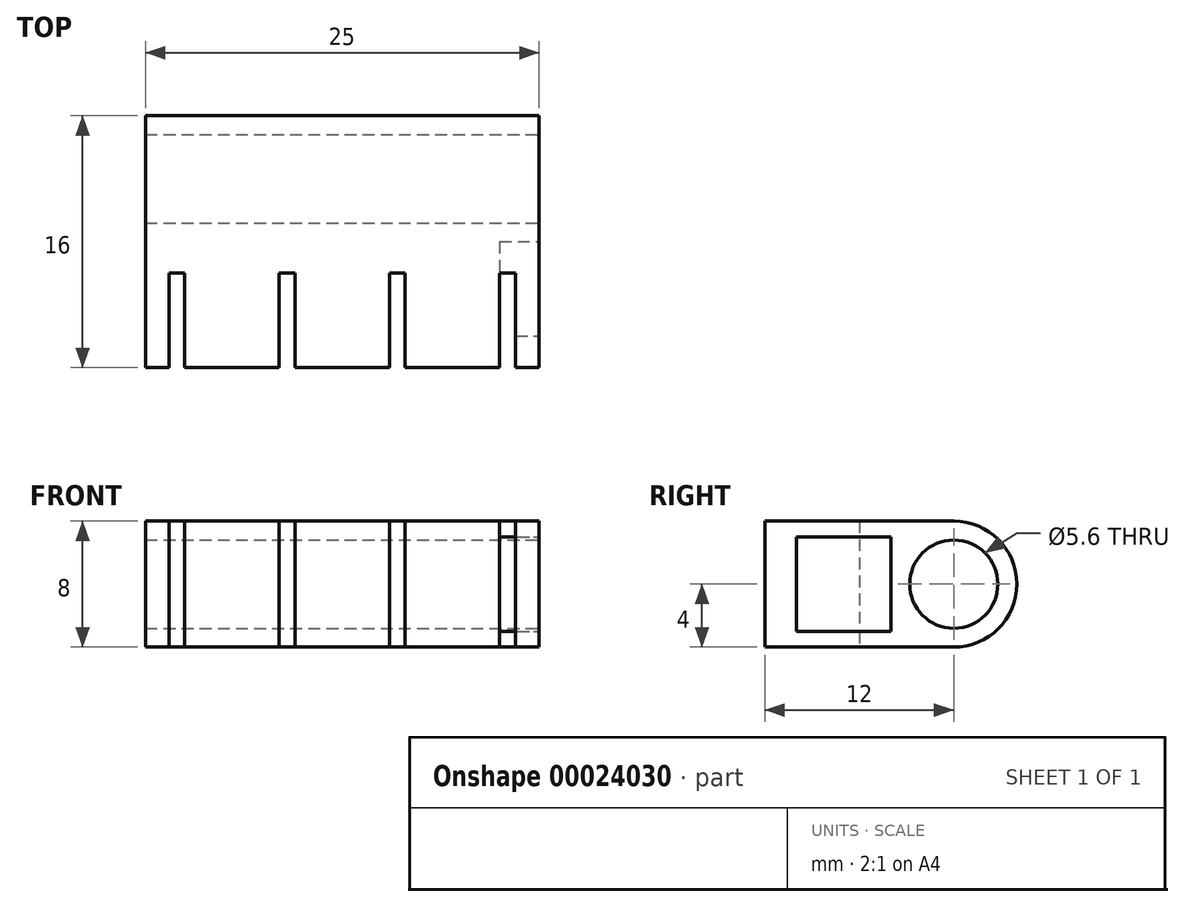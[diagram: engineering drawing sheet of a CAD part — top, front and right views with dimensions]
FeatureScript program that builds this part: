
annotation { "Feature Type Name" : "Feature", "Feature Type Description" : "" }
export const myFeature = defineFeature(function(context is Context, id is Id, definition is map)
    precondition{}
    {
        {
            var Q0;
            Q0=qCreatedBy(makeId("Top.planeOp"),FACE);
            var sketch = newSketch(context, id + "F0", { "sketchPlane" : qUnion([Q0])});
            skLineSegment(sketch, "E0.rect.bottom", {"start": v(-12.5, -5) * mm, "end": v(12.5, -5) * mm});
            skLineSegment(sketch, "E0.rect.top", {"start": v(-12.5, 5) * mm, "end": v(12.5, 5) * mm});
            skLineSegment(sketch, "E0.rect.left", {"start": v(-12.5, -5) * mm, "end": v(-12.5, 5) * mm});
            skLineSegment(sketch, "E0.rect.right", {"start": v(12.5, -5) * mm, "end": v(12.5, 5) * mm});
            skPoint(sketch, "E0.rect.middle", {"position": v(0, 0) * mm});
            skLineSegment(sketch, "E1.bottom", {"start": v(-3, -5) * mm, "end": v(-4, -5) * mm});
            skLineSegment(sketch, "E1.top", {"start": v(-3, 1) * mm, "end": v(-4, 1) * mm});
            skLineSegment(sketch, "E1.left", {"start": v(-3, -5) * mm, "end": v(-3, 1) * mm});
            skLineSegment(sketch, "E1.right", {"start": v(-4, -5) * mm, "end": v(-4, 1) * mm});
            skLineSegment(sketch, "E2.0.MirrorCS", {"start": v(3, -5) * mm, "end": v(3, 1) * mm});
            skLineSegment(sketch, "E3.0.MirrorCS", {"start": v(3, 1) * mm, "end": v(4, 1) * mm});
            skLineSegment(sketch, "E4.0.MirrorCS", {"start": v(4, -5) * mm, "end": v(4, 1) * mm});
            skLineSegment(sketch, "E5", {"start": v(-3.5, 1) * mm, "end": v(-3.5, -6.52) * mm, "construction": true});
            skLineSegment(sketch, "E6.0.MirrorCS", {"start": v(-10, -5) * mm, "end": v(-10, 1) * mm});
            skLineSegment(sketch, "E7.0.MirrorCS", {"start": v(-10, 1) * mm, "end": v(-11, 1) * mm});
            skLineSegment(sketch, "E8.0.MirrorCS", {"start": v(-11, -5) * mm, "end": v(-11, 1) * mm});
            skLineSegment(sketch, "E9", {"start": v(3.5, 1) * mm, "end": v(3.5, -5) * mm, "construction": true});
            skLineSegment(sketch, "E10.0.MirrorCS", {"start": v(11, -5) * mm, "end": v(11, 1) * mm});
            skLineSegment(sketch, "E11.0.MirrorCS", {"start": v(10, -5) * mm, "end": v(10, 1) * mm});
            skLineSegment(sketch, "E12.0.MirrorCS", {"start": v(10, 1) * mm, "end": v(11, 1) * mm});
            skSolve(sketch);
        }
        {
            var Q0;
            Q0=makeQuery(id+"F0.imprint","IMPRINT",FACE,{"disambiguationData":[TD([[makeQuery(id+"F0.imprint","IMPRINT",EDGE,{"derivedFrom":sQuery(id+"F0.wireOp",EDGE,"E0.rect.top")}),-1.0]])]});
            extrude(context, id + "F1", {"entities" : qUnion([Q0]), "depth" : 8 * mm});
        }
        {
            var Q0;
            Q0=makeQuery(id+"F1.opExtrude","SWEPT_FACE",FACE,{"disambiguationData":[OSD([sQuery(id+"F0.wireOp",EDGE,"E0.rect.right")])]});
            var sketch = newSketch(context, id + "F2", { "sketchPlane" : qUnion([Q0])});
            skLineSegment(sketch, "E13", {"start": v(5, 4) * mm, "end": v(-5, 4) * mm, "construction": true});
            skLineSegment(sketch, "E14", {"start": v(0, 8) * mm, "end": v(0, 0) * mm, "construction": true});
            skLineSegment(sketch, "E15.rect.bottom", {"start": v(3, 7) * mm, "end": v(-3, 7) * mm});
            skLineSegment(sketch, "E15.rect.top", {"start": v(3, 1) * mm, "end": v(-3, 1) * mm});
            skLineSegment(sketch, "E15.rect.left", {"start": v(3, 7) * mm, "end": v(3, 1) * mm});
            skLineSegment(sketch, "E15.rect.right", {"start": v(-3, 7) * mm, "end": v(-3, 1) * mm});
            skPoint(sketch, "E15.rect.middle", {"position": v(0, 4) * mm});
            skSolve(sketch);
        }
        {
            var Q0;
            Q0=makeQuery(id+"F2.imprint","IMPRINT",FACE,{"disambiguationData":[TD([[makeQuery(id+"F2.imprint","IMPRINT",EDGE,{"derivedFrom":sQuery(id+"F2.wireOp",EDGE,"E15.rect.bottom")}),1.0]])]});
            extrude(context, id + "F3", {"entities" : qUnion([Q0]), "operationType" : NewBodyOperationType.REMOVE, "oppositeDirection" : true, "depth" : 2.5 * mm});
        }
        {
            var Q0;
            Q0=makeQuery(id+"F1.opExtrude","SWEPT_FACE",FACE,{"disambiguationData":[OSD([sQuery(id+"F0.wireOp",EDGE,"E0.rect.top")])]});
            extrude(context, id + "F4", {"entities" : qUnion([Q0]), "operationType" : NewBodyOperationType.ADD, "depth" : 6 * mm});
        }
        {
            var Q0;
            {var subQ0=sQuery(id+"F0.wireOp",EDGE,"E0.rect.right");Q0=makeQuery(id+"F4.boolean.opBoolean","MERGE",FACE,{"derivedFrom":[makeQuery(id+"F1.opExtrude","SWEPT_FACE",FACE,{"disambiguationData":[OSD([subQ0])]}),makeQuery(id+"F4.opExtrude","SWEPT_FACE",FACE,{"disambiguationData":[OSD([sQuery(id+"F0.wireOp",EDGE,"E0.rect.top"),subQ0])]})]});}
            var sketch = newSketch(context, id + "F5", { "sketchPlane" : qUnion([Q0])});
            skLineSegment(sketch, "E16", {"start": v(11, 4) * mm, "end": v(3, 4) * mm, "construction": true});
            skPoint(sketch, "E16.endSnap0", {"position": v(3, 8) * mm});
            skLineSegment(sketch, "E17", {"start": v(7, 8) * mm, "end": v(7, 0) * mm, "construction": true});
            skPoint(sketch, "E18", {"position": v(7, 4) * mm});
            skSolve(sketch);
        }
        {
            var Q0;
            Q0=sQuery(id+"F5.wireOp",VERTEX,"E18");
            var Q1;
            Q1=makeQuery(id+"F1.opExtrude","SWEPT_BODY",BODY,{"disambiguationData":[OSD([sQuery(id+"F0.wireOp",EDGE,"E0.rect.bottom"),sQuery(id+"F0.wireOp",EDGE,"E0.rect.top"),sQuery(id+"F0.wireOp",EDGE,"E0.rect.left"),sQuery(id+"F0.wireOp",EDGE,"E0.rect.right"),sQuery(id+"F0.wireOp",EDGE,"E1.top"),sQuery(id+"F0.wireOp",EDGE,"E1.left"),sQuery(id+"F0.wireOp",EDGE,"E1.right"),sQuery(id+"F0.wireOp",EDGE,"E2.0.MirrorCS"),sQuery(id+"F0.wireOp",EDGE,"E3.0.MirrorCS"),sQuery(id+"F0.wireOp",EDGE,"E4.0.MirrorCS"),sQuery(id+"F0.wireOp",EDGE,"E6.0.MirrorCS"),sQuery(id+"F0.wireOp",EDGE,"E7.0.MirrorCS"),sQuery(id+"F0.wireOp",EDGE,"E8.0.MirrorCS"),sQuery(id+"F0.wireOp",EDGE,"E10.0.MirrorCS"),sQuery(id+"F0.wireOp",EDGE,"E11.0.MirrorCS"),sQuery(id+"F0.wireOp",EDGE,"E12.0.MirrorCS")])]});
            hole(context, id + "F6", {"style" : HoleStyle.SIMPLE, "endStyle" : HoleEndStyle.THROUGH, "holeDiameter" : 5.6 * mm, "locations" : qUnion([Q0]), "scope" : qUnion([Q1]), "isTappedThrough" : true});
        }
        {
            var Q0;
            {var subQ0=sQuery(id+"F0.wireOp",EDGE,"E0.rect.top");Q0=makeQuery(id+"F4.opExtrude","CAP_EDGE",EDGE,{"disambiguationData":[OSD([subQ0]),TDD([makeQuery(id+"F1.opExtrude","CAP_EDGE",EDGE,{"disambiguationData":[OSD([subQ0])],"isStart":true})])],"isStart":false});}
            var Q1;
            {var subQ0=sQuery(id+"F0.wireOp",EDGE,"E0.rect.top");Q1=makeQuery(id+"F4.opExtrude","CAP_EDGE",EDGE,{"disambiguationData":[OSD([subQ0]),TDD([makeQuery(id+"F1.opExtrude","CAP_EDGE",EDGE,{"disambiguationData":[OSD([subQ0])],"isStart":false})])],"isStart":false});}
            fillet(context, id + "F7", {"entities" : qUnion([Q0, Q1]), "radius" : 4 * mm, "tangentPropagation" : true, "allowEdgeOverflow" : false});
        }
    });
